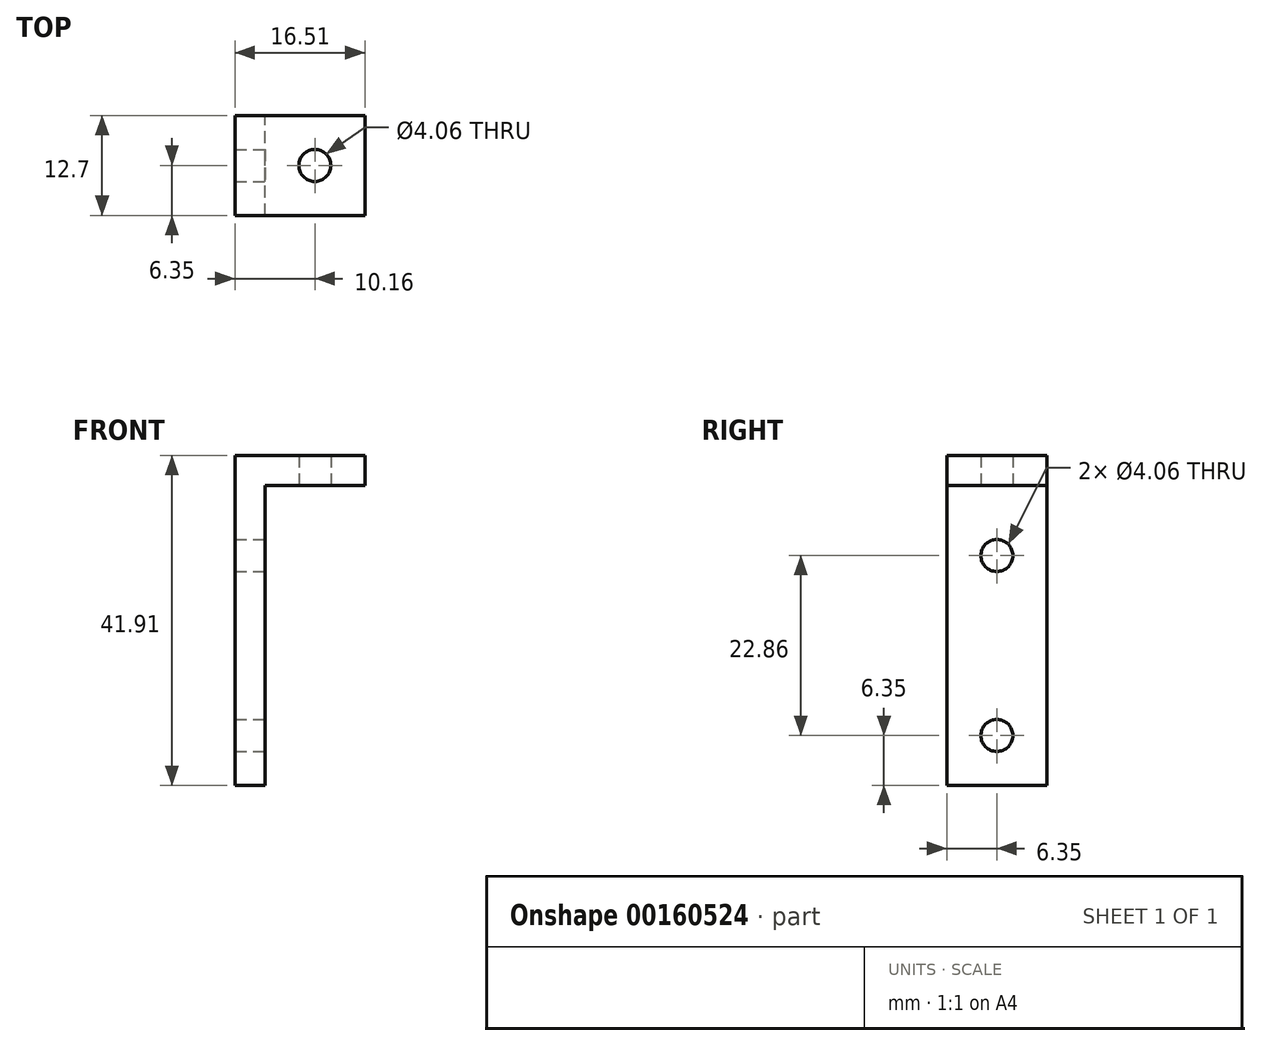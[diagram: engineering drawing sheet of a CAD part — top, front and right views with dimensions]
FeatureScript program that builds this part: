
annotation { "Feature Type Name" : "Feature", "Feature Type Description" : "" }
export const myFeature = defineFeature(function(context is Context, id is Id, definition is map)
    precondition{}
    {
        {
            var Q0;
            Q0=qCreatedBy(makeId("Front.planeOp"),FACE);
            var sketch = newSketch(context, id + "F0", { "sketchPlane" : qUnion([Q0])});
            skLineSegment(sketch, "E0.bottom", {"start": v(0, 0) * mm, "end": v(3.81, 0) * mm});
            skLineSegment(sketch, "E0.left", {"start": v(0, 0) * mm, "end": v(0, 41.9) * mm});
            skLineSegment(sketch, "E0.right", {"start": v(3.81, 0) * mm, "end": v(3.81, 38.1) * mm});
            skLineSegment(sketch, "E1.bottom", {"start": v(0, 41.9) * mm, "end": v(16.5, 41.9) * mm});
            skLineSegment(sketch, "E1.top", {"start": v(3.8, 38.1) * mm, "end": v(16.5, 38.1) * mm});
            skLineSegment(sketch, "E1.right", {"start": v(16.51, 41.9) * mm, "end": v(16.51, 38.1) * mm});
            skSolve(sketch);
        }
        {
            var Q0;
            Q0 = qSketchRegion(id + "F0", true);
            extrude(context, id + "F1", {"entities" : qUnion([Q0]), "depth" : 12.7 * mm});
        }
        {
            var Q0;
            Q0=makeQuery(id+"F1.opExtrude","SWEPT_FACE",FACE,{"disambiguationData":[OSD([sQuery(id+"F0.wireOp",EDGE,"E1.top")])]});
            var sketch = newSketch(context, id + "F2", { "sketchPlane" : qUnion([Q0])});
            skPoint(sketch, "E2", {"position": v(10.16, 6.35) * mm});
            skLineSegment(sketch, "E3", {"start": v(10.16, 6.35) * mm, "end": v(16.5, 6.35) * mm});
            skLineSegment(sketch, "E4", {"start": v(10.16, 6.35) * mm, "end": v(10.16, 12.7) * mm});
            skSolve(sketch);
        }
        {
            var Q0;
            Q0=sQuery(id+"F2.wireOp",VERTEX,"E2");
            var Q1;
            Q1=makeQuery(id+"F1.opExtrude","SWEPT_BODY",BODY,{"disambiguationData":[OSD([sQuery(id+"F0.wireOp",EDGE,"E0.bottom"),sQuery(id+"F0.wireOp",EDGE,"E0.left"),sQuery(id+"F0.wireOp",EDGE,"E0.right"),sQuery(id+"F0.wireOp",EDGE,"E1.bottom"),sQuery(id+"F0.wireOp",EDGE,"E1.top"),sQuery(id+"F0.wireOp",EDGE,"E1.right")])]});
            hole(context, id + "F3", {"style" : HoleStyle.SIMPLE, "endStyle" : HoleEndStyle.THROUGH, "holeDiameter" : 4.06 * mm, "locations" : qUnion([Q0]), "scope" : qUnion([Q1]), "isTappedThrough" : true});
        }
        {
            var Q0;
            Q0=makeQuery(id+"F1.opExtrude","SWEPT_FACE",FACE,{"disambiguationData":[OSD([sQuery(id+"F0.wireOp",EDGE,"E0.right")])]});
            var sketch = newSketch(context, id + "F4", { "sketchPlane" : qUnion([Q0])});
            skLineSegment(sketch, "E5", {"start": v(-6.35, 0) * mm, "end": v(-6.35, 38.1) * mm});
            skPoint(sketch, "E6", {"position": v(-6.35, 29.21) * mm});
            skPoint(sketch, "E7", {"position": v(-6.35, 6.35) * mm});
            skSolve(sketch);
        }
        {
            var Q0;
            Q0=sQuery(id+"F4.wireOp",VERTEX,"E6");
            var Q1;
            Q1=sQuery(id+"F4.wireOp",VERTEX,"E7");
            var Q2;
            Q2=makeQuery(id+"F1.opExtrude","SWEPT_BODY",BODY,{"disambiguationData":[OSD([sQuery(id+"F0.wireOp",EDGE,"E0.bottom"),sQuery(id+"F0.wireOp",EDGE,"E0.left"),sQuery(id+"F0.wireOp",EDGE,"E0.right"),sQuery(id+"F0.wireOp",EDGE,"E1.bottom"),sQuery(id+"F0.wireOp",EDGE,"E1.top"),sQuery(id+"F0.wireOp",EDGE,"E1.right")])]});
            hole(context, id + "F5", {"style" : HoleStyle.SIMPLE, "endStyle" : HoleEndStyle.THROUGH, "holeDiameter" : 4.06 * mm, "locations" : qUnion([Q0, Q1]), "scope" : qUnion([Q2]), "isTappedThrough" : true});
        }
    });
